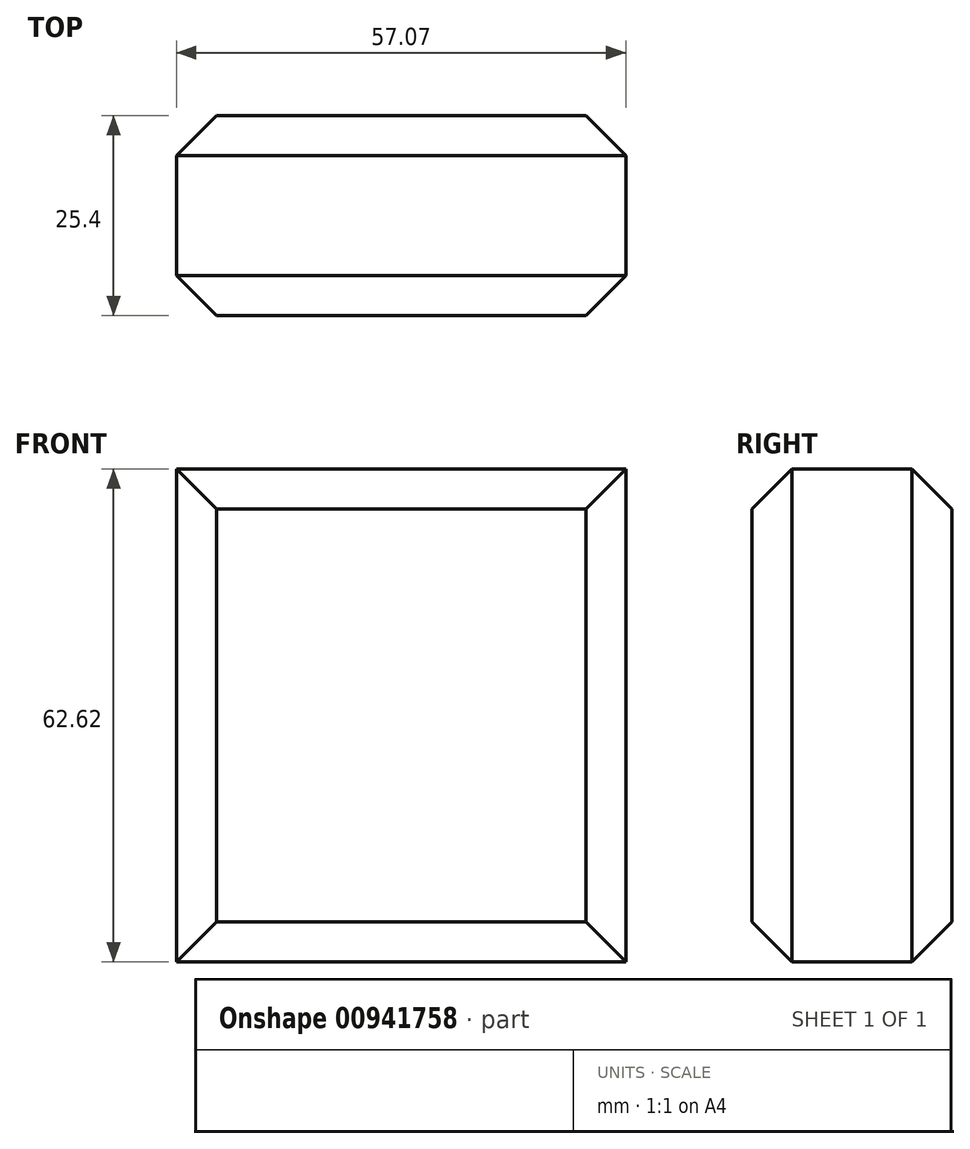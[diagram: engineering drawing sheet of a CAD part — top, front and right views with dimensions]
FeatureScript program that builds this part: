
annotation { "Feature Type Name" : "Feature", "Feature Type Description" : "" }
export const myFeature = defineFeature(function(context is Context, id is Id, definition is map)
    precondition{}
    {
        {
            var Q0;
            Q0=qCreatedBy(makeId("Front.planeOp"),FACE);
            var sketch = newSketch(context, id + "F0", { "sketchPlane" : qUnion([Q0])});
            skLineSegment(sketch, "E0.bottom", {"start": v(-126.16, 49.19) * mm, "end": v(-69.1, 49.19) * mm});
            skLineSegment(sketch, "E0.top", {"start": v(-126.16, -13.43) * mm, "end": v(-69.1, -13.43) * mm});
            skLineSegment(sketch, "E0.left", {"start": v(-126.16, 49.19) * mm, "end": v(-126.16, -13.43) * mm});
            skLineSegment(sketch, "E0.right", {"start": v(-69.1, 49.19) * mm, "end": v(-69.1, -13.43) * mm});
            skLineSegment(sketch, "E1.bottom", {"start": v(-63.59, -17.34) * mm, "end": v(-49.97, -17.34) * mm});
            skLineSegment(sketch, "E1.top", {"start": v(-63.59, -24.42) * mm, "end": v(-49.97, -24.42) * mm});
            skLineSegment(sketch, "E1.left", {"start": v(-63.59, -17.34) * mm, "end": v(-63.59, -24.42) * mm});
            skLineSegment(sketch, "E1.right", {"start": v(-49.97, -17.34) * mm, "end": v(-49.97, -24.42) * mm});
            skSolve(sketch);
        }
        {
            var Q0;
            Q0 = qSketchRegion(id + "F0", true);
            extrude(context, id + "F1", {"entities" : qUnion([Q0]), "depth" : 25.4 * mm, "offsetDistance" : 25.4 * mm});
        }
        {
            var Q0;
            Q0=makeQuery(id+"F1.opExtrude","SWEPT_BODY",BODY,{"disambiguationData":[OSD([sQuery(id+"F0.wireOp",EDGE,"E1.bottom"),sQuery(id+"F0.wireOp",EDGE,"E1.top"),sQuery(id+"F0.wireOp",EDGE,"E1.left"),sQuery(id+"F0.wireOp",EDGE,"E1.right")])]});
            deleteBodies(context, id + "F2", {"entities" : qUnion([Q0])});
        }
        {
            var Q0;
            Q0=makeQuery(id+"F1.opExtrude","CAP_FACE",FACE,{"disambiguationData":[OSD([sQuery(id+"F0.wireOp",EDGE,"E0.bottom"),sQuery(id+"F0.wireOp",EDGE,"E0.top"),sQuery(id+"F0.wireOp",EDGE,"E0.left"),sQuery(id+"F0.wireOp",EDGE,"E0.right")])],"isStart":false});
            var Q1;
            Q1=makeQuery(id+"F1.opExtrude","CAP_FACE",FACE,{"disambiguationData":[OSD([sQuery(id+"F0.wireOp",EDGE,"E0.bottom"),sQuery(id+"F0.wireOp",EDGE,"E0.top"),sQuery(id+"F0.wireOp",EDGE,"E0.left"),sQuery(id+"F0.wireOp",EDGE,"E0.right")])],"isStart":true});
            chamfer(context, id + "F3", {"entities" : qUnion([Q0, Q1]), "width" : 5.08 * mm, "tangentPropagation" : true});
        }
    });
